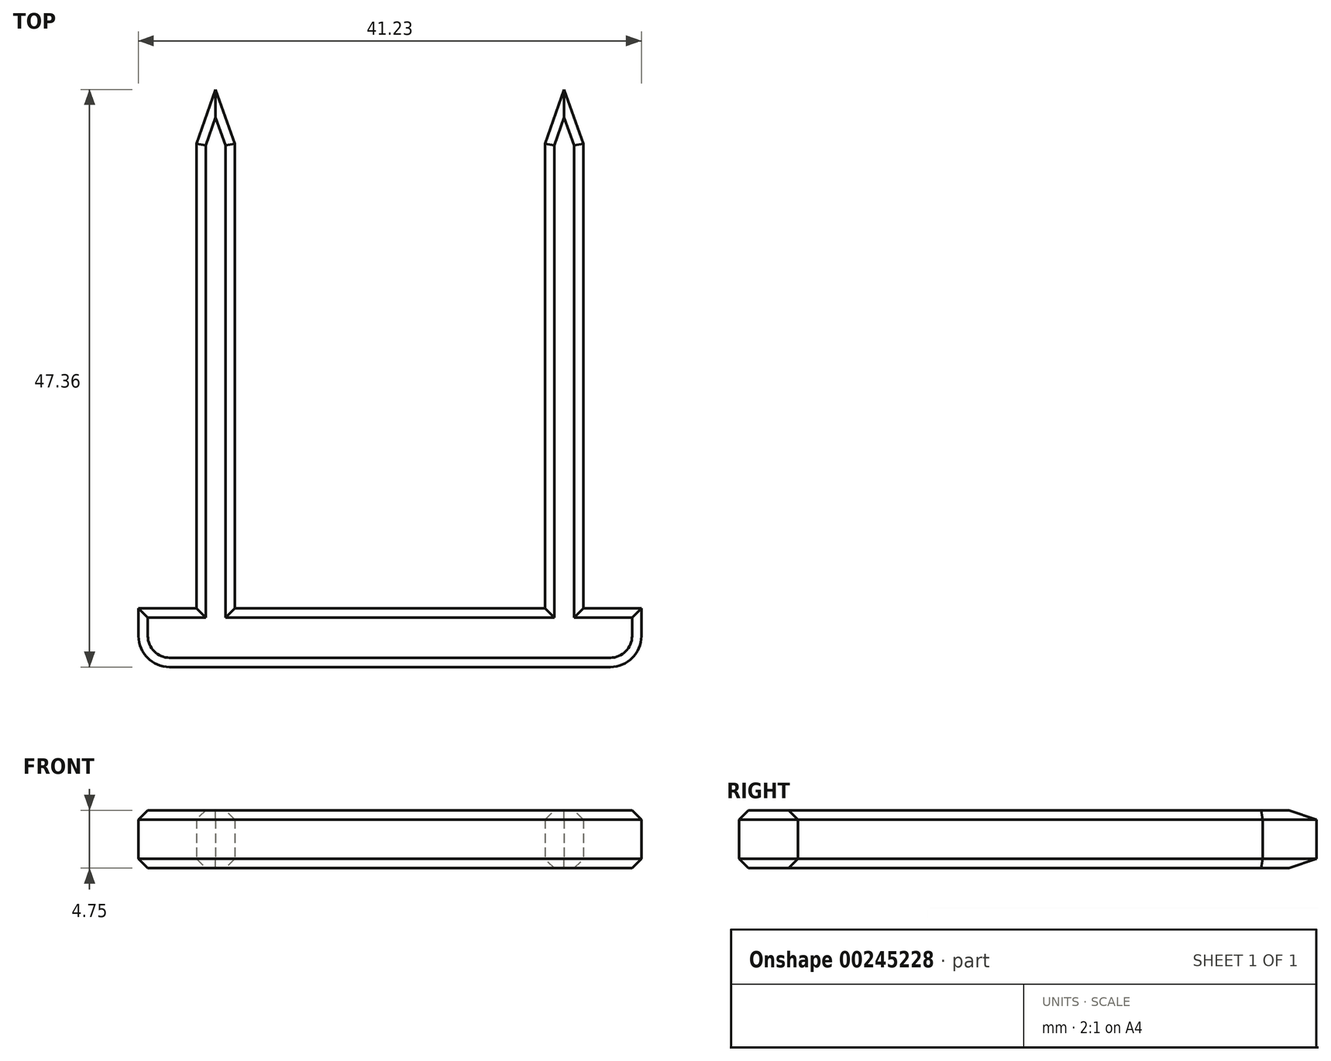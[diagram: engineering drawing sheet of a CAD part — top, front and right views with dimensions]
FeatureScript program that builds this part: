
annotation { "Feature Type Name" : "Feature", "Feature Type Description" : "" }
export const myFeature = defineFeature(function(context is Context, id is Id, definition is map)
    precondition{}
    {
        {
            var Q0;
            Q0=qCreatedBy(makeId("Top.planeOp"),FACE);
            var sketch = newSketch(context, id + "F0", { "sketchPlane" : qUnion([Q0])});
            skLineSegment(sketch, "E0.bottom", {"start": v(-12.03, -25.41) * mm, "end": v(16.54, -25.41) * mm});
            skLineSegment(sketch, "E0.top", {"start": v(-12.03, 12.69) * mm, "end": v(-10.46, 12.69) * mm});
            skLineSegment(sketch, "E0.left", {"start": v(-12.03, -25.41) * mm, "end": v(-12.03, 12.69) * mm});
            skLineSegment(sketch, "E0.right", {"start": v(16.54, -25.41) * mm, "end": v(16.54, 12.69) * mm});
            skLineSegment(sketch, "E1.0", {"start": v(-10.46, -25.41) * mm, "end": v(-10.46, 12.69) * mm});
            skLineSegment(sketch, "E2.0", {"start": v(-13.6, -25.41) * mm, "end": v(-13.6, 12.69) * mm});
            skLineSegment(sketch, "E3.0", {"start": v(18.12, -25.41) * mm, "end": v(18.12, 12.69) * mm});
            skLineSegment(sketch, "E4.0", {"start": v(14.97, -25.41) * mm, "end": v(14.97, 12.69) * mm});
            skLineSegment(sketch, "E5.trimOffspring", {"start": v(14.97, 12.69) * mm, "end": v(16.54, 12.69) * mm});
            skLineSegment(sketch, "E6", {"start": v(-12.03, 12.69) * mm, "end": v(-12.03, 17.12) * mm});
            skLineSegment(sketch, "E7", {"start": v(16.54, 17.12) * mm, "end": v(16.54, 12.69) * mm});
            skLineSegment(sketch, "E8", {"start": v(-13.6, 12.69) * mm, "end": v(-12.03, 17.12) * mm});
            skLineSegment(sketch, "E9", {"start": v(-10.46, 12.69) * mm, "end": v(-12.03, 17.12) * mm});
            skLineSegment(sketch, "E10", {"start": v(14.97, 12.69) * mm, "end": v(16.54, 17.12) * mm});
            skLineSegment(sketch, "E11", {"start": v(18.12, 12.69) * mm, "end": v(16.54, 17.12) * mm});
            skLineSegment(sketch, "E12", {"start": v(-13.6, -25.41) * mm, "end": v(-18.36, -25.41) * mm});
            skLineSegment(sketch, "E13", {"start": v(-18.36, -25.41) * mm, "end": v(-18.36, -27.7) * mm});
            skLineSegment(sketch, "E14", {"start": v(-15.82, -30.24) * mm, "end": v(20.33, -30.24) * mm});
            skLineSegment(sketch, "E15", {"start": v(22.87, -27.7) * mm, "end": v(22.87, -25.41) * mm});
            skLineSegment(sketch, "E16", {"start": v(22.87, -25.41) * mm, "end": v(18.12, -25.41) * mm});
            skPoint(sketch, "E17.visualSharp", {"position": v(22.87, -30.24) * mm});
            skArc(sketch, "E17.filletArc", {"start": v(20.33, -30.24) * mm, "mid": v(22.12, -29.5) * mm, "end": v(22.87, -27.7) * mm});
            skPoint(sketch, "E18.visualSharp", {"position": v(-18.36, -30.24) * mm});
            skArc(sketch, "E18.filletArc", {"start": v(-18.36, -27.7) * mm, "mid": v(-17.61, -29.5) * mm, "end": v(-15.82, -30.24) * mm});
            skSolve(sketch);
        }
        {
            var Q0;
            Q0 = qSketchRegion(id + "FJKji5fgEIEqfwCNo_0", true);
            var Q1;
            Q1=makeQuery(id+"F0.imprint","IMPRINT",FACE,{"disambiguationData":[TD([[makeQuery(id+"F0.imprint","IMPRINT",EDGE,{"derivedFrom":sQuery(id+"F0.wireOp",EDGE,"E0.top")}),-1.0]])]});
            var Q2;
            {var subQ0=sQuery(id+"F0.wireOp",EDGE,"E0.left");Q2=makeQuery(id+"F0.imprint","IMPRINT",FACE,{"disambiguationData":[TD([[makeQuery(id+"F0.imprint","IMPRINT",EDGE,{"derivedFrom":subQ0}),1.0]])]});}
            var Q3;
            {var subQ0=sQuery(id+"F0.wireOp",EDGE,"E0.right");Q3=makeQuery(id+"F0.imprint","IMPRINT",FACE,{"disambiguationData":[TD([[makeQuery(id+"F0.imprint","IMPRINT",EDGE,{"derivedFrom":subQ0}),1.0]])]});}
            var Q4;
            Q4=makeQuery(id+"F0.imprint","IMPRINT",FACE,{"disambiguationData":[TD([[makeQuery(id+"F0.imprint","IMPRINT",EDGE,{"derivedFrom":sQuery(id+"F0.wireOp",EDGE,"E0.top")}),1.0]])]});
            var Q5;
            Q5=makeQuery(id+"F0.imprint","IMPRINT",FACE,{"disambiguationData":[TD([[makeQuery(id+"F0.imprint","IMPRINT",EDGE,{"derivedFrom":sQuery(id+"F0.wireOp",EDGE,"E5.trimOffspring")}),1.0]])]});
            extrude(context, id + "F1", {"entities" : qUnion([Q0, Q1, Q2, Q3, Q4, Q5]), "depth" : 4.75 * mm});
        }
        {
            var Q0;
            Q0=makeQuery(id+"F1.opExtrude","CAP_EDGE",EDGE,{"disambiguationData":[OSD([sQuery(id+"F0.wireOp",EDGE,"E2.0")])],"isStart":false});
            var Q1;
            Q1=makeQuery(id+"F1.opExtrude","CAP_FACE",FACE,{"disambiguationData":[OSD([sQuery(id+"F0.wireOp",EDGE,"E0.bottom"),sQuery(id+"F0.wireOp",EDGE,"E1.0"),sQuery(id+"F0.wireOp",EDGE,"E2.0"),sQuery(id+"F0.wireOp",EDGE,"E3.0"),sQuery(id+"F0.wireOp",EDGE,"E4.0"),sQuery(id+"F0.wireOp",EDGE,"E8"),sQuery(id+"F0.wireOp",EDGE,"E9"),sQuery(id+"F0.wireOp",EDGE,"E10"),sQuery(id+"F0.wireOp",EDGE,"E11"),sQuery(id+"F0.wireOp",EDGE,"E12"),sQuery(id+"F0.wireOp",EDGE,"E13"),sQuery(id+"F0.wireOp",EDGE,"E14"),sQuery(id+"F0.wireOp",EDGE,"E15"),sQuery(id+"F0.wireOp",EDGE,"E16"),sQuery(id+"F0.wireOp",EDGE,"E17.filletArc"),sQuery(id+"F0.wireOp",EDGE,"E18.filletArc")])],"isStart":false});
            var Q2;
            Q2=makeQuery(id+"F1.opExtrude","CAP_FACE",FACE,{"disambiguationData":[OSD([sQuery(id+"F0.wireOp",EDGE,"E0.bottom"),sQuery(id+"F0.wireOp",EDGE,"E1.0"),sQuery(id+"F0.wireOp",EDGE,"E2.0"),sQuery(id+"F0.wireOp",EDGE,"E3.0"),sQuery(id+"F0.wireOp",EDGE,"E4.0"),sQuery(id+"F0.wireOp",EDGE,"E8"),sQuery(id+"F0.wireOp",EDGE,"E9"),sQuery(id+"F0.wireOp",EDGE,"E10"),sQuery(id+"F0.wireOp",EDGE,"E11"),sQuery(id+"F0.wireOp",EDGE,"E12"),sQuery(id+"F0.wireOp",EDGE,"E13"),sQuery(id+"F0.wireOp",EDGE,"E14"),sQuery(id+"F0.wireOp",EDGE,"E15"),sQuery(id+"F0.wireOp",EDGE,"E16"),sQuery(id+"F0.wireOp",EDGE,"E17.filletArc"),sQuery(id+"F0.wireOp",EDGE,"E18.filletArc")])],"isStart":true});
            chamfer(context, id + "F2", {"entities" : qUnion([Q0, Q1, Q2]), "width" : 0.76 * mm, "tangentPropagation" : true});
        }
    });
